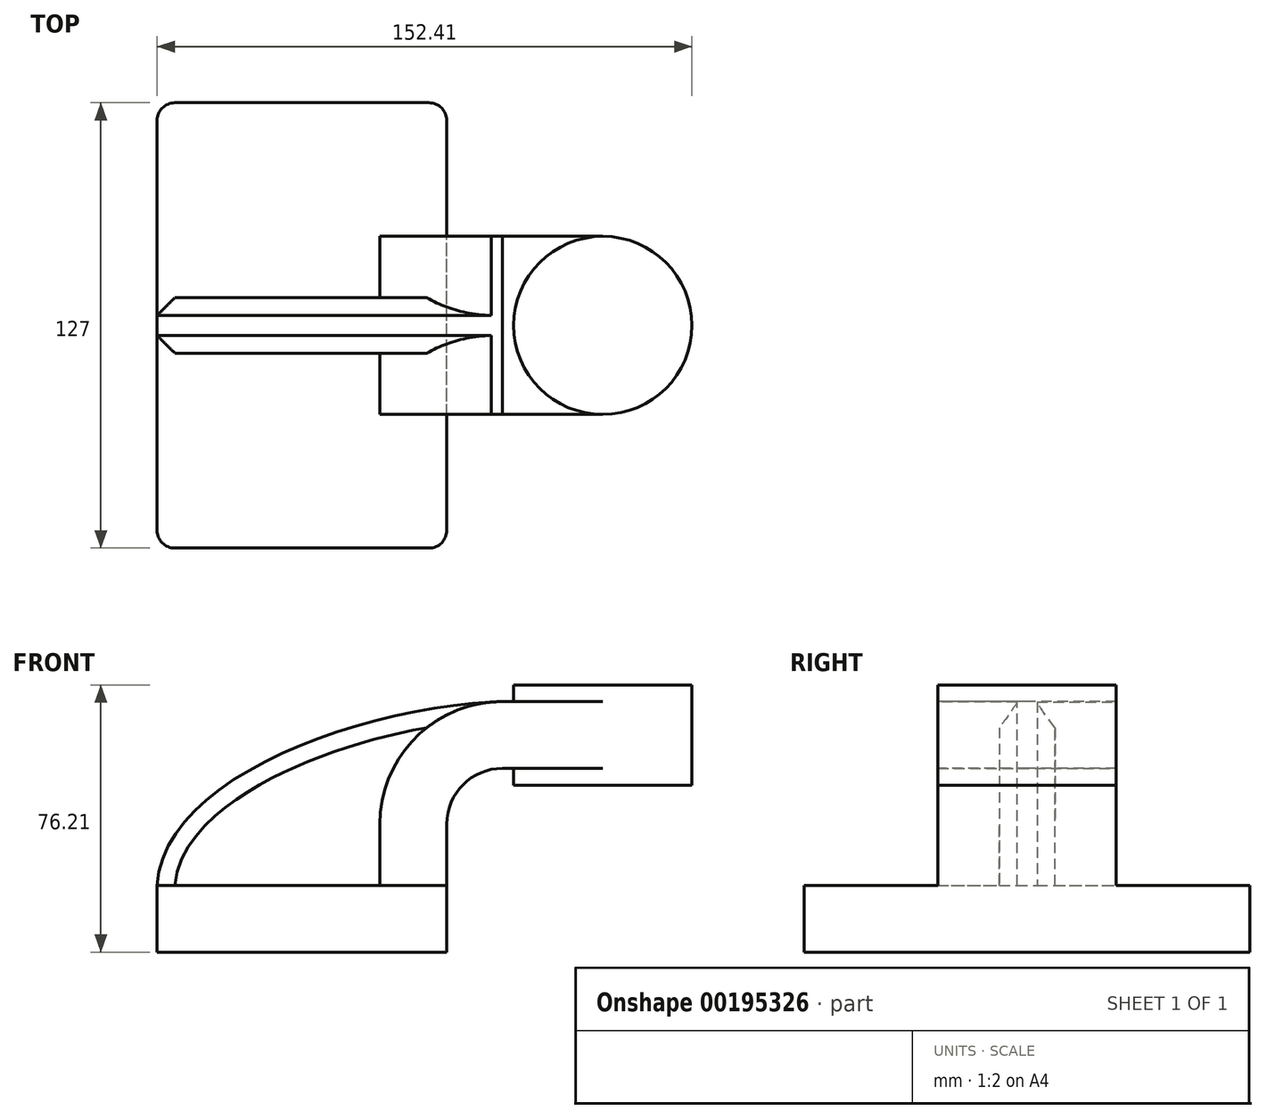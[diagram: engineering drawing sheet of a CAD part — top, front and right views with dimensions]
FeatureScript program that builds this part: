
annotation { "Feature Type Name" : "Feature", "Feature Type Description" : "" }
export const myFeature = defineFeature(function(context is Context, id is Id, definition is map)
    precondition{}
    {
        {
            var Q0;
            Q0=qCreatedBy(makeId("Front.planeOp"),FACE);
            var sketch = newSketch(context, id + "F0", { "sketchPlane" : qUnion([Q0])});
            skLineSegment(sketch, "E0.rect.bottom", {"start": v(-41.28, 9.52) * mm, "end": v(41.28, 9.52) * mm});
            skLineSegment(sketch, "E0.rect.top", {"start": v(-41.28, -9.52) * mm, "end": v(41.28, -9.52) * mm});
            skLineSegment(sketch, "E0.rect.left", {"start": v(-41.28, 9.52) * mm, "end": v(-41.28, -9.52) * mm});
            skLineSegment(sketch, "E0.rect.right", {"start": v(41.28, 9.52) * mm, "end": v(41.28, -9.52) * mm});
            skPoint(sketch, "E0.rect.middle", {"position": v(0, 0) * mm});
            skLineSegment(sketch, "E1", {"start": v(41.28, 9.52) * mm, "end": v(41.28, 27) * mm});
            skArc(sketch, "E2", {"start": v(41.28, 27) * mm, "mid": v(45.92, 38.23) * mm, "end": v(57.15, 42.88) * mm});
            skLineSegment(sketch, "E3", {"start": v(57.15, 42.88) * mm, "end": v(85.72, 42.88) * mm});
            skLineSegment(sketch, "E4.rect.bottom", {"start": v(60.32, 38.1) * mm, "end": v(111.12, 38.1) * mm});
            skLineSegment(sketch, "E4.rect.top", {"start": v(60.32, 66.68) * mm, "end": v(111.12, 66.68) * mm});
            skLineSegment(sketch, "E4.rect.left", {"start": v(60.32, 38.1) * mm, "end": v(60.32, 66.68) * mm});
            skLineSegment(sketch, "E4.rect.right", {"start": v(111.13, 38.1) * mm, "end": v(111.12, 66.68) * mm});
            skPoint(sketch, "E4.rect.middle", {"position": v(85.72, 52.39) * mm});
            skLineSegment(sketch, "E5.0", {"start": v(57.15, 61.93) * mm, "end": v(85.72, 61.93) * mm});
            skArc(sketch, "E5.1", {"start": v(22.23, 27) * mm, "mid": v(32.45, 51.7) * mm, "end": v(57.15, 61.93) * mm});
            skLineSegment(sketch, "E5.2", {"start": v(22.23, 9.52) * mm, "end": v(22.23, 27) * mm});
            skLineSegment(sketch, "E6", {"start": v(85.72, 38.1) * mm, "end": v(85.72, 66.68) * mm});
            skFitSpline(sketch, "E7", {"points": [v(-41.28, 9.53) * mm, v(57.15, 61.93) * mm], "startDerivative": vector(5.2, 92.34) * mm, "endDerivative": vector(120.92, 4.22) * mm});
            skSolve(sketch);
        }
        {
            var Q0;
            Q0=makeQuery(id+"F0.imprint","IMPRINT",FACE,{"disambiguationData":[TD([[makeQuery(id+"F0.imprint","IMPRINT",EDGE,{"derivedFrom":sQuery(id+"F0.wireOp",EDGE,"E0.rect.top")}),1.0]])]});
            extrude(context, id + "F1", {"entities" : qUnion([Q0]), "endBound" : BoundingType.SYMMETRIC, "depth" : 127 * mm});
        }
        {
            var Q0;
            {var subQ9=sQuery(id+"F0.wireOp",EDGE,"E1");Q0=makeQuery(id+"F0.imprint","IMPRINT",FACE,{"disambiguationData":[TD([[makeQuery(id+"F0.imprint","IMPRINT",EDGE,{"derivedFrom":subQ9}),1.0]])]});}
            var Q1;
            {var subQ0=sQuery(id+"F0.wireOp",EDGE,"E6");var subQ1=sQuery(id+"F0.wireOp",EDGE,"E3");var subQ2=makeQuery(id+"F0.imprint","INTERSECT",VERTEX,{"derivedFrom":[subQ1,subQ0]});Q1=makeQuery(id+"F0.imprint","IMPRINT",FACE,{"disambiguationData":[TD([[makeQuery(id+"F0.imprint","IMPRINT",EDGE,{"disambiguationData":[TD([[subQ2,1.0]])],"derivedFrom":subQ1}),1.0]])]});}
            extrude(context, id + "F2", {"entities" : qUnion([Q0, Q1]), "operationType" : NewBodyOperationType.ADD, "endBound" : BoundingType.SYMMETRIC, "depth" : 50.8 * mm});
        }
        {
            var Q0;
            {var subQ3=sQuery(id+"F0.wireOp",EDGE,"E5.2");Q0=makeQuery(id+"F0.imprint","IMPRINT",FACE,{"disambiguationData":[TD([[makeQuery(id+"F0.imprint","IMPRINT",EDGE,{"derivedFrom":subQ3}),1.0]])]});}
            extrude(context, id + "F3", {"entities" : qUnion([Q0]), "operationType" : NewBodyOperationType.ADD, "endBound" : BoundingType.SYMMETRIC, "depth" : 15.88 * mm});
        }
        {
            var Q0;
            {var subQ5=sQuery(id+"F0.wireOp",EDGE,"E4.rect.right");Q0=makeQuery(id+"F0.imprint","IMPRINT",FACE,{"disambiguationData":[TD([[makeQuery(id+"F0.imprint","IMPRINT",EDGE,{"derivedFrom":subQ5}),1.0]])]});}
            var Q1;
            Q1=sQuery(id+"F0.wireOp",EDGE,"E6");
            revolve(context, id + "F4", {"operationType" : NewBodyOperationType.ADD, "entities" : qUnion([Q0]), "axis" : qUnion([Q1]), "revolveType" : RevolveType.FULL});
        }
        {
            var Q0;
            Q0=makeQuery(id+"F1.opExtrude","CAP_EDGE",EDGE,{"disambiguationData":[OSD([sQuery(id+"F0.wireOp",EDGE,"E0.rect.right")])],"isStart":false});
            var Q1;
            Q1=makeQuery(id+"F1.opExtrude","CAP_EDGE",EDGE,{"disambiguationData":[OSD([sQuery(id+"F0.wireOp",EDGE,"E0.rect.left")])],"isStart":false});
            var Q2;
            Q2=makeQuery(id+"F1.opExtrude","CAP_EDGE",EDGE,{"disambiguationData":[OSD([sQuery(id+"F0.wireOp",EDGE,"E0.rect.right")])],"isStart":true});
            var Q3;
            Q3=makeQuery(id+"F1.opExtrude","CAP_EDGE",EDGE,{"disambiguationData":[OSD([sQuery(id+"F0.wireOp",EDGE,"E0.rect.left")])],"isStart":true});
            fillet(context, id + "F5", {"entities" : qUnion([Q0, Q1, Q2, Q3]), "radius" : 5.08 * mm, "tangentPropagation" : true, "allowEdgeOverflow" : false});
        }
        {
            var Q0;
            Q0=makeQuery(id+"F3.opExtrude","CAP_EDGE",EDGE,{"disambiguationData":[OSD([sQuery(id+"F0.wireOp",EDGE,"E7")])],"isStart":false});
            chamfer(context, id + "F6", {"entities" : qUnion([Q0]), "width" : 5.08 * mm, "tangentPropagation" : true});
        }
        {
            var Q0;
            Q0=makeQuery(id+"F3.opExtrude","CAP_EDGE",EDGE,{"disambiguationData":[OSD([sQuery(id+"F0.wireOp",EDGE,"E7")])],"isStart":true});
            chamfer(context, id + "F7", {"entities" : qUnion([Q0]), "width" : 5.08 * mm, "tangentPropagation" : true});
        }
    });
